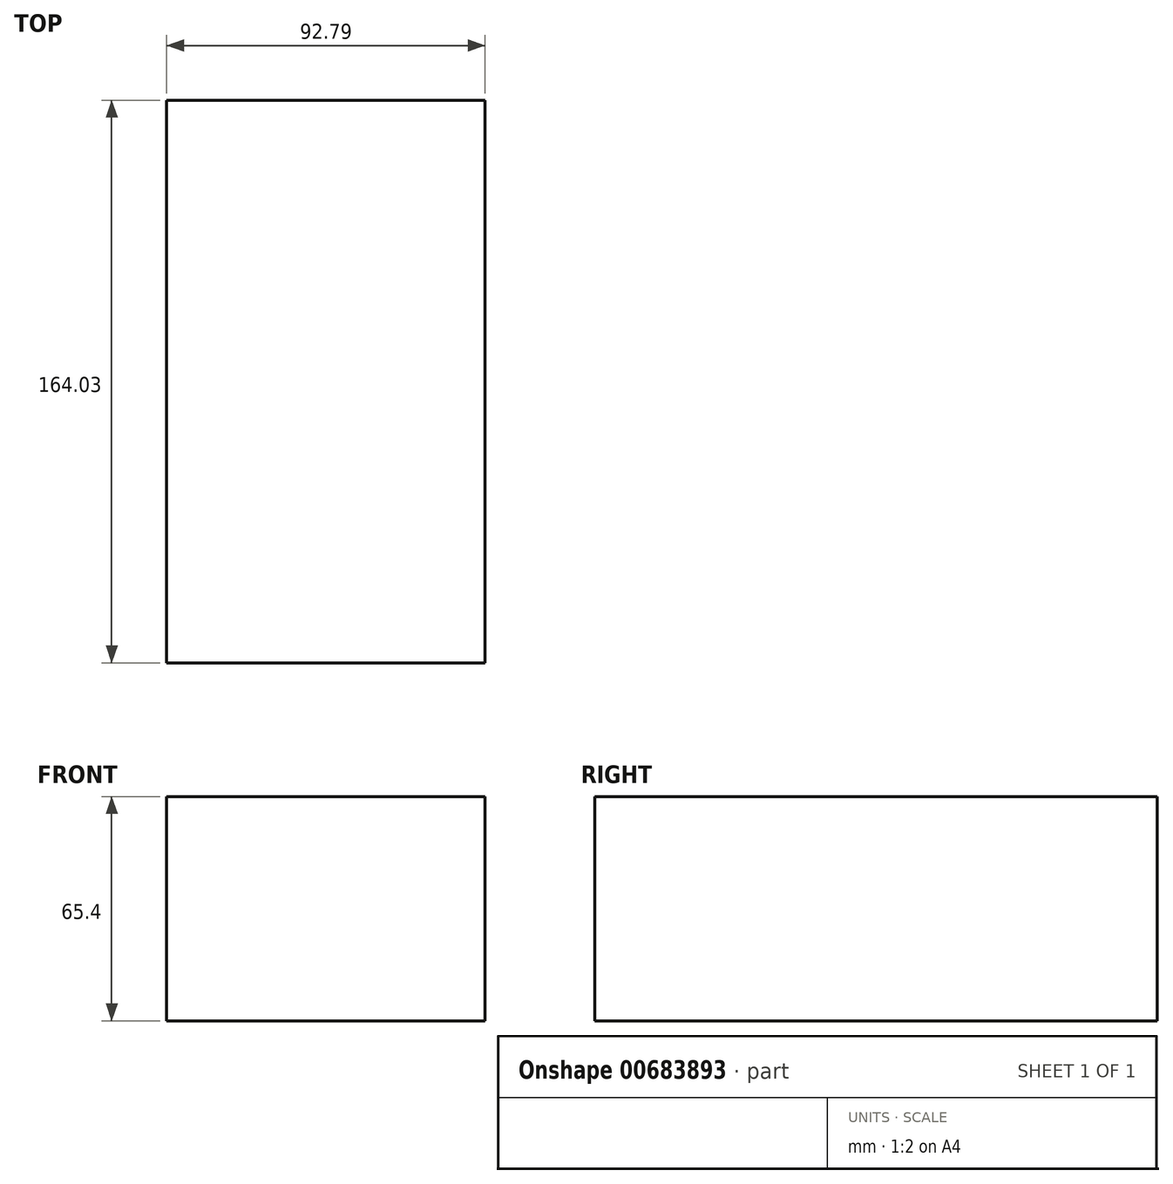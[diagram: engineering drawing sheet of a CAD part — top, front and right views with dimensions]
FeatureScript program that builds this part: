
annotation { "Feature Type Name" : "Feature", "Feature Type Description" : "" }
export const myFeature = defineFeature(function(context is Context, id is Id, definition is map)
    precondition{}
    {
        {
            var Q0;
            Q0=qCreatedBy(makeId("Top.planeOp"),FACE);
            var sketch = newSketch(context, id + "F0", { "sketchPlane" : qUnion([Q0])});
            skLineSegment(sketch, "E0.bottom", {"start": v(0, 68.72) * mm, "end": v(92.79, 68.72) * mm});
            skLineSegment(sketch, "E0.top", {"start": v(0, -95.3) * mm, "end": v(92.79, -95.3) * mm});
            skLineSegment(sketch, "E0.left", {"start": v(0, 68.72) * mm, "end": v(0, -95.3) * mm});
            skLineSegment(sketch, "E0.right", {"start": v(92.79, 68.72) * mm, "end": v(92.79, -95.3) * mm});
            skSolve(sketch);
        }
        {
            var Q0;
            Q0 = qSketchRegion(id + "F0", true);
            extrude(context, id + "F1", {"entities" : qUnion([Q0]), "depth" : 65.4 * mm, "offsetDistance" : 25.4 * mm});
        }
    });
